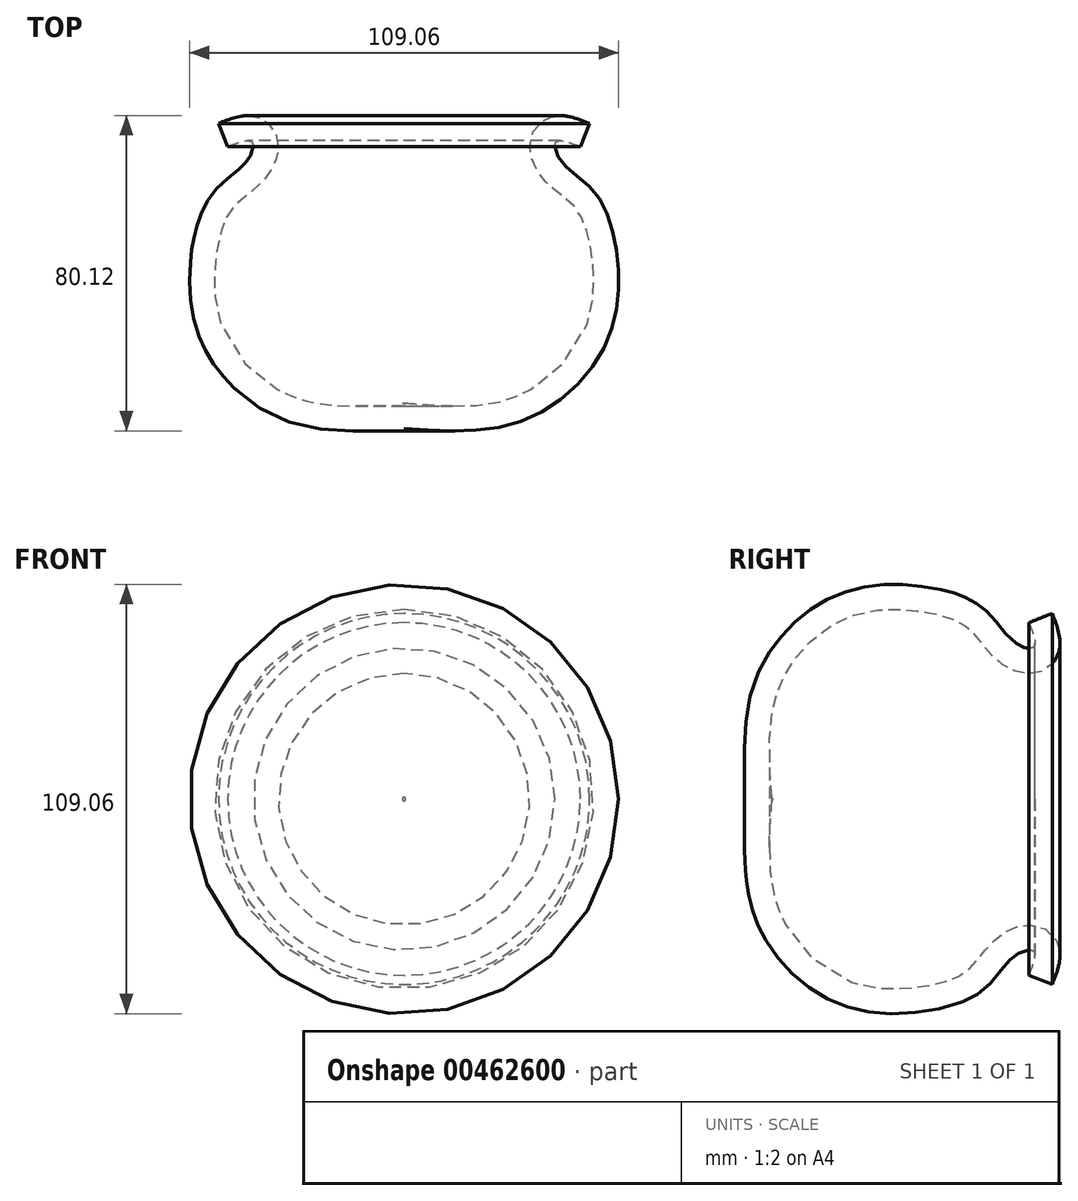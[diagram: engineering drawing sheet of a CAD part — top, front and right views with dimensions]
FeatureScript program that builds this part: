
annotation { "Feature Type Name" : "Feature", "Feature Type Description" : "" }
export const myFeature = defineFeature(function(context is Context, id is Id, definition is map)
    precondition{}
    {
        {
            var Q0;
            Q0=qCreatedBy(makeId("Top.planeOp"),FACE);
            var sketch = newSketch(context, id + "F0", { "sketchPlane" : qUnion([Q0])});
            skLineSegment(sketch, "E0", {"start": v(0, 53.5) * mm, "end": v(0, -55.02) * mm});
            skFitSpline(sketch, "E1", {"points": [v(0, -46.79) * mm, v(30.48, -44.65) * mm, v(50.9, -26.06) * mm, v(54.25, -4.11) * mm, v(48.46, 13.26) * mm, v(39.62, 21.49) * mm, v(38.7, 26.06) * mm, v(44.8, 24.84) * mm], "startDerivative": vector(160.43, -10.97) * mm, "endDerivative": vector(86.97, -34.3) * mm});
            skFitSpline(sketch, "E2.0", {"points": [v(0.43, -40.45) * mm, v(3.78, -40.68) * mm, v(8.67, -41.01) * mm, v(14.8, -41.06) * mm, v(19.15, -40.81) * mm, v(22.55, -40.33) * mm, v(25.13, -39.73) * mm, v(26.68, -39.28) * mm, v(27.88, -38.85) * mm, v(29.06, -38.4) * mm, v(30.53, -37.73) * mm, v(32.27, -36.8) * mm, v(34.52, -35.4) * mm, v(37.21, -33.37) * mm, v(40.13, -30.58) * mm, v(42.65, -27.55) * mm, v(44.7, -24.38) * mm, v(46.2, -21.23) * mm, v(47.24, -17.97) * mm, v(47.9, -14.6) * mm, v(48.15, -11.7) * mm, v(48.19, -9.34) * mm, v(48.14, -7.54) * mm, v(48.03, -5.72) * mm, v(47.86, -3.88) * mm, v(47.62, -2.08) * mm, v(47.24, 0.25) * mm, v(46.73, 2.43) * mm, v(46.1, 4.4) * mm, v(45.58, 5.76) * mm, v(45.02, 6.98) * mm, v(44.51, 7.88) * mm, v(44.1, 8.51) * mm, v(43.84, 8.88) * mm, v(43.62, 9.15) * mm, v(43.41, 9.4) * mm, v(43.12, 9.73) * mm, v(42.73, 10.14) * mm, v(42.15, 10.68) * mm, v(41.34, 11.39) * mm, v(40.22, 12.29) * mm, v(38.98, 13.26) * mm, v(37.66, 14.35) * mm, v(36.5, 15.4) * mm, v(35.57, 16.4) * mm, v(34.99, 17.08) * mm, v(34.54, 17.68) * mm, v(34.1, 18.3) * mm, v(33.61, 19.1) * mm, v(33.1, 20.1) * mm, v(32.68, 21.11) * mm, v(32.33, 22.18) * mm, v(32.08, 23.32) * mm, v(31.94, 24.6) * mm, v(31.98, 25.8) * mm, v(32.18, 26.91) * mm, v(32.44, 27.81) * mm, v(32.86, 28.77) * mm, v(33.38, 29.59) * mm, v(33.9, 30.22) * mm, v(34.34, 30.68) * mm, v(34.82, 31.1) * mm, v(35.5, 31.58) * mm, v(36.36, 32.05) * mm, v(37.34, 32.4) * mm, v(38.23, 32.6) * mm, v(39.3, 32.73) * mm, v(40.4, 32.7) * mm, v(41.51, 32.57) * mm, v(42.47, 32.36) * mm, v(43.35, 32.12) * mm, v(44.18, 31.86) * mm, v(44.96, 31.58) * mm, v(45.97, 31.2) * mm, v(46.68, 30.93) * mm, v(47.14, 30.75) * mm]});
            skFitSpline(sketch, "E3", {"points": [v(47.14, 30.75) * mm, v(44.8, 24.84) * mm], "startDerivative": vector(-2.33, -5.9) * mm, "endDerivative": vector(-2.33, -5.9) * mm});
            skFitSpline(sketch, "E4", {"points": [v(0.43, -40.45) * mm, v(-11.28, -36.73) * mm], "startDerivative": vector(-11.71, 3.72) * mm, "endDerivative": vector(-11.71, 3.72) * mm});
            skSolve(sketch);
        }
        {
            var Q0;
            Q0 = qSketchRegion(id + "F0", true);
            var Q1;
            Q1=sQuery(id+"F0.wireOp",EDGE,"E0");
            revolve(context, id + "F1", {"entities" : qUnion([Q0]), "axis" : qUnion([Q1]), "revolveType" : RevolveType.FULL});
        }
    });
